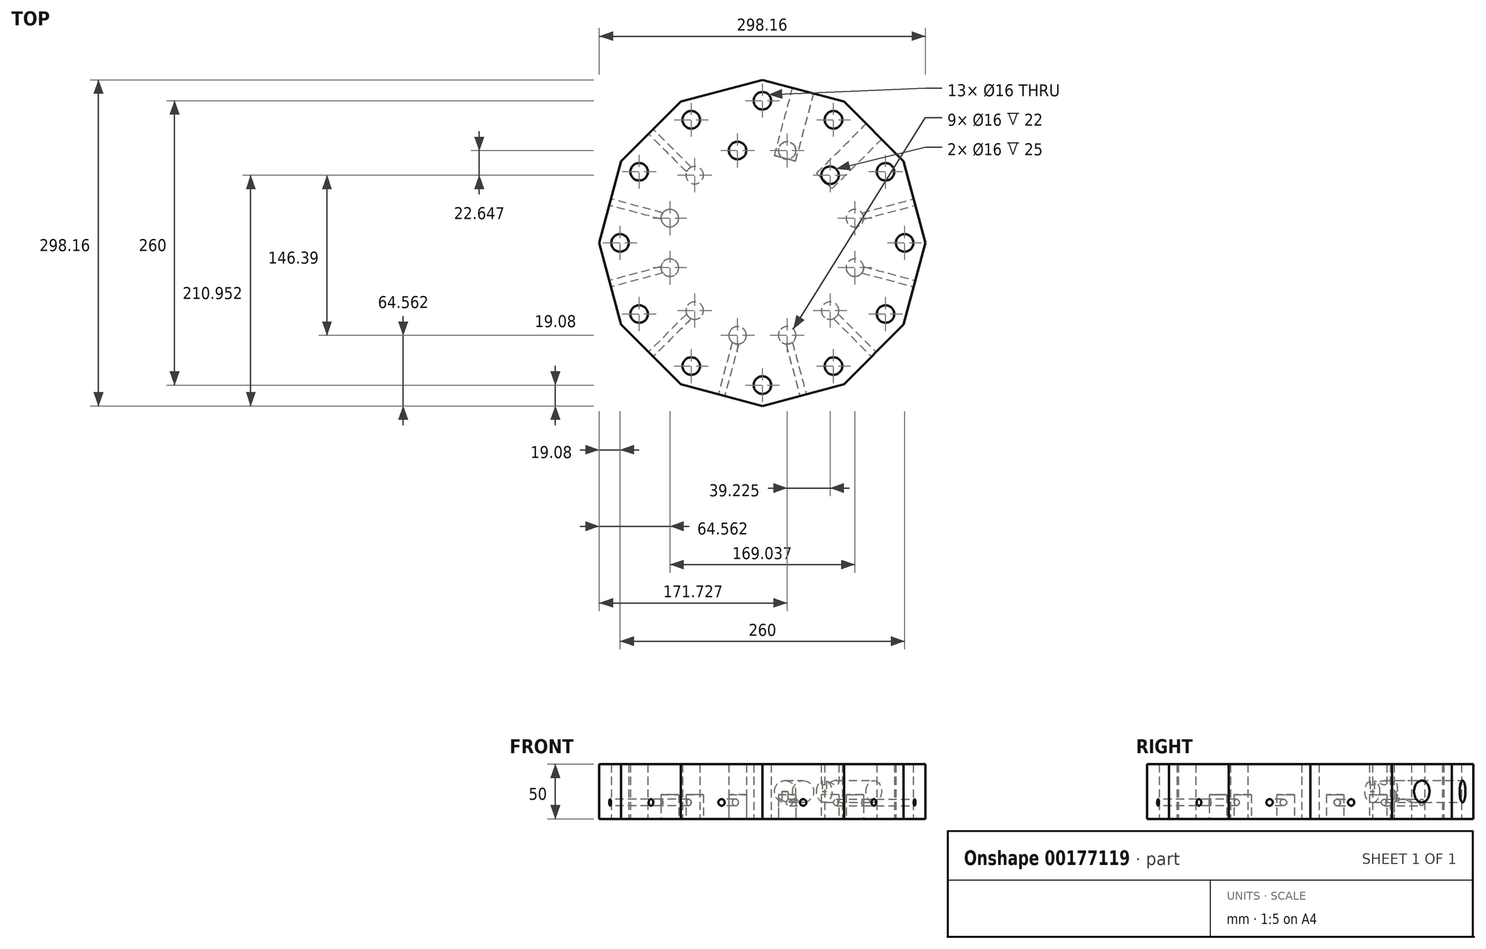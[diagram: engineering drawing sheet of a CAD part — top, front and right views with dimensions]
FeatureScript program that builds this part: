
annotation { "Feature Type Name" : "Feature", "Feature Type Description" : "" }
export const myFeature = defineFeature(function(context is Context, id is Id, definition is map)
    precondition{}
    {
        {
            var Q0;
            Q0=qCreatedBy(makeId("Top.planeOp"),FACE);
            var sketch = newSketch(context, id + "F0", { "sketchPlane" : qUnion([Q0])});
            skCircle(sketch, "E0.cCircle", {"center": v(0, 0) * mm, "radius": 144 * mm, "construction": true});
            skLineSegment(sketch, "E0.0", {"start": v(-74.54, 129.1) * mm, "end": v(0, 149.08) * mm});
            skLineSegment(sketch, "E0.1", {"start": v(0, 149.08) * mm, "end": v(74.54, 129.1) * mm});
            skLineSegment(sketch, "E0.2", {"start": v(74.54, 129.1) * mm, "end": v(129.1, 74.54) * mm});
            skLineSegment(sketch, "E0.3", {"start": v(129.1, 74.54) * mm, "end": v(149.08, 0) * mm});
            skLineSegment(sketch, "E0.4", {"start": v(149.08, 0) * mm, "end": v(129.1, -74.54) * mm});
            skLineSegment(sketch, "E0.5", {"start": v(129.1, -74.54) * mm, "end": v(74.54, -129.1) * mm});
            skLineSegment(sketch, "E0.6", {"start": v(74.54, -129.1) * mm, "end": v(0, -149.08) * mm});
            skLineSegment(sketch, "E0.7", {"start": v(0, -149.08) * mm, "end": v(-74.54, -129.1) * mm});
            skLineSegment(sketch, "E0.8", {"start": v(-74.54, -129.1) * mm, "end": v(-129.1, -74.54) * mm});
            skLineSegment(sketch, "E0.9", {"start": v(-129.1, -74.54) * mm, "end": v(-149.08, 0) * mm});
            skLineSegment(sketch, "E0.10", {"start": v(-149.08, 0) * mm, "end": v(-129.1, 74.54) * mm});
            skLineSegment(sketch, "E0.11", {"start": v(-129.1, 74.54) * mm, "end": v(-74.54, 129.1) * mm});
            skPoint(sketch, "E0.0.midPoint", {"position": v(-37.27, 139.1) * mm});
            skPoint(sketch, "E1.endSnap0", {"position": v(-101.82, 101.82) * mm});
            skSolve(sketch);
        }
        {
            var Q0;
            Q0=makeQuery(id+"F0.imprint","IMPRINT",FACE,{"disambiguationData":[TD([[makeQuery(id+"F0.imprint","IMPRINT",EDGE,{"derivedFrom":sQuery(id+"F0.wireOp",EDGE,"E0.0")}),-1.0]])]});
            extrude(context, id + "F1", {"entities" : qUnion([Q0]), "depth" : 50 * mm});
        }
        {
            var Q0;
            Q0=qCreatedBy(makeId("Top.planeOp"),FACE);
            var sketch = newSketch(context, id + "F2", { "sketchPlane" : qUnion([Q0])});
            skCircle(sketch, "E2", {"center": v(0, 130) * mm, "radius": 8 * mm});
            skCircle(sketch, "E3", {"center": v(22.65, 84.52) * mm, "radius": 8 * mm});
            skLineSegment(sketch, "E4", {"start": v(0, 0) * mm, "end": v(22.65, 84.52) * mm, "construction": true});
            skLineSegment(sketch, "E5", {"start": v(0, 0) * mm, "end": v(-22.65, 84.52) * mm, "construction": true});
            skCircle(sketch, "E6", {"center": v(-22.65, 84.52) * mm, "radius": 8 * mm});
            skCircle(sketch, "E7", {"center": v(61.87, 61.87) * mm, "radius": 8 * mm});
            skLineSegment(sketch, "E8", {"start": v(0, 0) * mm, "end": v(61.87, 61.87) * mm, "construction": true});
            skCircle(sketch, "E9", {"center": v(-61.87, 61.87) * mm, "radius": 8 * mm});
            skLineSegment(sketch, "E10", {"start": v(0, 0) * mm, "end": v(-61.87, 61.87) * mm, "construction": true});
            skCircle(sketch, "E11", {"center": v(0, 0) * mm, "radius": 87.5 * mm, "construction": true});
            skSolve(sketch);
        }
        {
            var Q0;
            Q0=makeQuery(id+"F2.imprint","IMPRINT",FACE,{"disambiguationData":[TD([[makeQuery(id+"F2.imprint","IMPRINT",EDGE,{"derivedFrom":sQuery(id+"F2.wireOp",EDGE,"E2")}),1.0]])]});
            extrude(context, id + "F3", {"entities" : qUnion([Q0]), "depth" : 50 * mm});
        }
        {
            var Q0;
            Q0=makeQuery(id+"F3.opExtrude","SWEPT_BODY",BODY,{"disambiguationData":[OSD([sQuery(id+"F2.wireOp",EDGE,"E2")])]});
            var Q1;
            Q1=sQuery(id+"F0.wireOp",EDGE,"E0.cCircle");
            circularPattern(context, id + "F4", {"entities" : qUnion([Q0]), "axis" : qUnion([Q1]), "angle" : 30 * degree, "instanceCount" : 12});
        }
        {
            var Q0;
            Q0=makeQuery(id+"F2.imprint","IMPRINT",FACE,{"disambiguationData":[TD([[makeQuery(id+"F2.imprint","IMPRINT",EDGE,{"derivedFrom":sQuery(id+"F2.wireOp",EDGE,"E6")}),1.0]])]});
            extrude(context, id + "F5", {"entities" : qUnion([Q0]), "operationType" : NewBodyOperationType.REMOVE, "endBound" : BoundingType.THROUGH_ALL, "depth" : 25 * mm});
        }
        {
            var Q0;
            Q0=makeQuery(id+"F2.imprint","IMPRINT",FACE,{"disambiguationData":[TD([[makeQuery(id+"F2.imprint","IMPRINT",EDGE,{"derivedFrom":sQuery(id+"F2.wireOp",EDGE,"E3")}),1.0]])]});
            extrude(context, id + "F6", {"entities" : qUnion([Q0]), "operationType" : NewBodyOperationType.REMOVE, "depth" : 25 * mm});
        }
        {
            var Q0;
            Q0=makeQuery(id+"F2.imprint","IMPRINT",FACE,{"disambiguationData":[TD([[makeQuery(id+"F2.imprint","IMPRINT",EDGE,{"derivedFrom":sQuery(id+"F2.wireOp",EDGE,"E7")}),1.0]])]});
            extrude(context, id + "F7", {"entities" : qUnion([Q0]), "operationType" : NewBodyOperationType.REMOVE, "depth" : 50 * mm, "hasSecondDirection" : true, "secondDirectionOppositeDirection" : false, "secondDirectionDepth" : 25 * mm});
        }
        {
            var Q0;
            Q0=makeQuery(id+"F4.opPattern","COPY",BODY,{"derivedFrom":makeQuery(id+"F3.opExtrude","SWEPT_BODY",BODY,{"disambiguationData":[OSD([sQuery(id+"F2.wireOp",EDGE,"E2")])]}),"instanceName":"11"});
            var Q1;
            Q1=makeQuery(id+"F4.opPattern","COPY",BODY,{"derivedFrom":makeQuery(id+"F3.opExtrude","SWEPT_BODY",BODY,{"disambiguationData":[OSD([sQuery(id+"F2.wireOp",EDGE,"E2")])]}),"instanceName":"10"});
            var Q2;
            Q2=makeQuery(id+"F4.opPattern","COPY",BODY,{"derivedFrom":makeQuery(id+"F3.opExtrude","SWEPT_BODY",BODY,{"disambiguationData":[OSD([sQuery(id+"F2.wireOp",EDGE,"E2")])]}),"instanceName":"9"});
            var Q3;
            Q3=makeQuery(id+"F4.opPattern","COPY",BODY,{"derivedFrom":makeQuery(id+"F3.opExtrude","SWEPT_BODY",BODY,{"disambiguationData":[OSD([sQuery(id+"F2.wireOp",EDGE,"E2")])]}),"instanceName":"8"});
            var Q4;
            Q4=makeQuery(id+"F4.opPattern","COPY",BODY,{"derivedFrom":makeQuery(id+"F3.opExtrude","SWEPT_BODY",BODY,{"disambiguationData":[OSD([sQuery(id+"F2.wireOp",EDGE,"E2")])]}),"instanceName":"7"});
            var Q5;
            Q5=makeQuery(id+"F4.opPattern","COPY",BODY,{"derivedFrom":makeQuery(id+"F3.opExtrude","SWEPT_BODY",BODY,{"disambiguationData":[OSD([sQuery(id+"F2.wireOp",EDGE,"E2")])]}),"instanceName":"6"});
            var Q6;
            Q6=makeQuery(id+"F4.opPattern","COPY",BODY,{"derivedFrom":makeQuery(id+"F3.opExtrude","SWEPT_BODY",BODY,{"disambiguationData":[OSD([sQuery(id+"F2.wireOp",EDGE,"E2")])]}),"instanceName":"5"});
            var Q7;
            Q7=makeQuery(id+"F4.opPattern","COPY",BODY,{"derivedFrom":makeQuery(id+"F3.opExtrude","SWEPT_BODY",BODY,{"disambiguationData":[OSD([sQuery(id+"F2.wireOp",EDGE,"E2")])]}),"instanceName":"4"});
            var Q8;
            Q8=makeQuery(id+"F4.opPattern","COPY",BODY,{"derivedFrom":makeQuery(id+"F3.opExtrude","SWEPT_BODY",BODY,{"disambiguationData":[OSD([sQuery(id+"F2.wireOp",EDGE,"E2")])]}),"instanceName":"3"});
            var Q9;
            Q9=makeQuery(id+"F4.opPattern","COPY",BODY,{"derivedFrom":makeQuery(id+"F3.opExtrude","SWEPT_BODY",BODY,{"disambiguationData":[OSD([sQuery(id+"F2.wireOp",EDGE,"E2")])]}),"instanceName":"2"});
            var Q10;
            Q10=makeQuery(id+"F4.opPattern","COPY",BODY,{"derivedFrom":makeQuery(id+"F3.opExtrude","SWEPT_BODY",BODY,{"disambiguationData":[OSD([sQuery(id+"F2.wireOp",EDGE,"E2")])]}),"instanceName":"1"});
            var Q11;
            Q11=makeQuery(id+"F3.opExtrude","SWEPT_BODY",BODY,{"disambiguationData":[OSD([sQuery(id+"F2.wireOp",EDGE,"E2")])]});
            var Q12;
            Q12=makeQuery(id+"FBsRg0TL2h17wES_2.opPattern","COPY",BODY,{"derivedFrom":makeQuery(id+"FloVHYxQ3IDST4M_1.opRevolve","SWEPT_BODY",BODY,{"disambiguationData":[OSD([sQuery(id+"FTWyRQ9hsPiHUXF_1.wireOp",EDGE,"gz86ioHb-P1qW-ang3-GePB-rddx3RvaeM8G"),sQuery(id+"FTWyRQ9hsPiHUXF_1.wireOp",EDGE,"9s4MmS5F-P29b-mFub-vPlP-xrfaxyTz5IiV"),sQuery(id+"FTWyRQ9hsPiHUXF_1.wireOp",EDGE,"ncLqOzuC-NzLh-Ri5l-9KgU-PrjhPgCbsoXL"),sQuery(id+"FTWyRQ9hsPiHUXF_1.wireOp",EDGE,"QWZmu36O-cUKC-ijbu-LDt6-pPJv8b1BSPT7"),sQuery(id+"FTWyRQ9hsPiHUXF_1.wireOp",EDGE,"U38Iat36-SeyG-4MAB-tlqH-BICu5RhWfs5p"),sQuery(id+"FTWyRQ9hsPiHUXF_1.wireOp",EDGE,"ujRQtfkf-Bo7a-oEIA-ZBmy-LZaghkBHRdtm")])]}),"instanceName":"8"});
            var Q13;
            Q13=makeQuery(id+"FBsRg0TL2h17wES_2.opPattern","COPY",BODY,{"derivedFrom":makeQuery(id+"FloVHYxQ3IDST4M_1.opRevolve","SWEPT_BODY",BODY,{"disambiguationData":[OSD([sQuery(id+"FTWyRQ9hsPiHUXF_1.wireOp",EDGE,"gz86ioHb-P1qW-ang3-GePB-rddx3RvaeM8G"),sQuery(id+"FTWyRQ9hsPiHUXF_1.wireOp",EDGE,"9s4MmS5F-P29b-mFub-vPlP-xrfaxyTz5IiV"),sQuery(id+"FTWyRQ9hsPiHUXF_1.wireOp",EDGE,"ncLqOzuC-NzLh-Ri5l-9KgU-PrjhPgCbsoXL"),sQuery(id+"FTWyRQ9hsPiHUXF_1.wireOp",EDGE,"QWZmu36O-cUKC-ijbu-LDt6-pPJv8b1BSPT7"),sQuery(id+"FTWyRQ9hsPiHUXF_1.wireOp",EDGE,"U38Iat36-SeyG-4MAB-tlqH-BICu5RhWfs5p"),sQuery(id+"FTWyRQ9hsPiHUXF_1.wireOp",EDGE,"ujRQtfkf-Bo7a-oEIA-ZBmy-LZaghkBHRdtm")])]}),"instanceName":"7"});
            var Q14;
            Q14=makeQuery(id+"FBsRg0TL2h17wES_2.opPattern","COPY",BODY,{"derivedFrom":makeQuery(id+"FloVHYxQ3IDST4M_1.opRevolve","SWEPT_BODY",BODY,{"disambiguationData":[OSD([sQuery(id+"FTWyRQ9hsPiHUXF_1.wireOp",EDGE,"gz86ioHb-P1qW-ang3-GePB-rddx3RvaeM8G"),sQuery(id+"FTWyRQ9hsPiHUXF_1.wireOp",EDGE,"9s4MmS5F-P29b-mFub-vPlP-xrfaxyTz5IiV"),sQuery(id+"FTWyRQ9hsPiHUXF_1.wireOp",EDGE,"ncLqOzuC-NzLh-Ri5l-9KgU-PrjhPgCbsoXL"),sQuery(id+"FTWyRQ9hsPiHUXF_1.wireOp",EDGE,"QWZmu36O-cUKC-ijbu-LDt6-pPJv8b1BSPT7"),sQuery(id+"FTWyRQ9hsPiHUXF_1.wireOp",EDGE,"U38Iat36-SeyG-4MAB-tlqH-BICu5RhWfs5p"),sQuery(id+"FTWyRQ9hsPiHUXF_1.wireOp",EDGE,"ujRQtfkf-Bo7a-oEIA-ZBmy-LZaghkBHRdtm")])]}),"instanceName":"6"});
            var Q15;
            Q15=makeQuery(id+"FBsRg0TL2h17wES_2.opPattern","COPY",BODY,{"derivedFrom":makeQuery(id+"FloVHYxQ3IDST4M_1.opRevolve","SWEPT_BODY",BODY,{"disambiguationData":[OSD([sQuery(id+"FTWyRQ9hsPiHUXF_1.wireOp",EDGE,"gz86ioHb-P1qW-ang3-GePB-rddx3RvaeM8G"),sQuery(id+"FTWyRQ9hsPiHUXF_1.wireOp",EDGE,"9s4MmS5F-P29b-mFub-vPlP-xrfaxyTz5IiV"),sQuery(id+"FTWyRQ9hsPiHUXF_1.wireOp",EDGE,"ncLqOzuC-NzLh-Ri5l-9KgU-PrjhPgCbsoXL"),sQuery(id+"FTWyRQ9hsPiHUXF_1.wireOp",EDGE,"QWZmu36O-cUKC-ijbu-LDt6-pPJv8b1BSPT7"),sQuery(id+"FTWyRQ9hsPiHUXF_1.wireOp",EDGE,"U38Iat36-SeyG-4MAB-tlqH-BICu5RhWfs5p"),sQuery(id+"FTWyRQ9hsPiHUXF_1.wireOp",EDGE,"ujRQtfkf-Bo7a-oEIA-ZBmy-LZaghkBHRdtm")])]}),"instanceName":"5"});
            var Q16;
            Q16=makeQuery(id+"FBsRg0TL2h17wES_2.opPattern","COPY",BODY,{"derivedFrom":makeQuery(id+"FloVHYxQ3IDST4M_1.opRevolve","SWEPT_BODY",BODY,{"disambiguationData":[OSD([sQuery(id+"FTWyRQ9hsPiHUXF_1.wireOp",EDGE,"gz86ioHb-P1qW-ang3-GePB-rddx3RvaeM8G"),sQuery(id+"FTWyRQ9hsPiHUXF_1.wireOp",EDGE,"9s4MmS5F-P29b-mFub-vPlP-xrfaxyTz5IiV"),sQuery(id+"FTWyRQ9hsPiHUXF_1.wireOp",EDGE,"ncLqOzuC-NzLh-Ri5l-9KgU-PrjhPgCbsoXL"),sQuery(id+"FTWyRQ9hsPiHUXF_1.wireOp",EDGE,"QWZmu36O-cUKC-ijbu-LDt6-pPJv8b1BSPT7"),sQuery(id+"FTWyRQ9hsPiHUXF_1.wireOp",EDGE,"U38Iat36-SeyG-4MAB-tlqH-BICu5RhWfs5p"),sQuery(id+"FTWyRQ9hsPiHUXF_1.wireOp",EDGE,"ujRQtfkf-Bo7a-oEIA-ZBmy-LZaghkBHRdtm")])]}),"instanceName":"4"});
            var Q17;
            Q17=makeQuery(id+"FBsRg0TL2h17wES_2.opPattern","COPY",BODY,{"derivedFrom":makeQuery(id+"FloVHYxQ3IDST4M_1.opRevolve","SWEPT_BODY",BODY,{"disambiguationData":[OSD([sQuery(id+"FTWyRQ9hsPiHUXF_1.wireOp",EDGE,"gz86ioHb-P1qW-ang3-GePB-rddx3RvaeM8G"),sQuery(id+"FTWyRQ9hsPiHUXF_1.wireOp",EDGE,"9s4MmS5F-P29b-mFub-vPlP-xrfaxyTz5IiV"),sQuery(id+"FTWyRQ9hsPiHUXF_1.wireOp",EDGE,"ncLqOzuC-NzLh-Ri5l-9KgU-PrjhPgCbsoXL"),sQuery(id+"FTWyRQ9hsPiHUXF_1.wireOp",EDGE,"QWZmu36O-cUKC-ijbu-LDt6-pPJv8b1BSPT7"),sQuery(id+"FTWyRQ9hsPiHUXF_1.wireOp",EDGE,"U38Iat36-SeyG-4MAB-tlqH-BICu5RhWfs5p"),sQuery(id+"FTWyRQ9hsPiHUXF_1.wireOp",EDGE,"ujRQtfkf-Bo7a-oEIA-ZBmy-LZaghkBHRdtm")])]}),"instanceName":"3"});
            var Q18;
            Q18=makeQuery(id+"FBsRg0TL2h17wES_2.opPattern","COPY",BODY,{"derivedFrom":makeQuery(id+"FloVHYxQ3IDST4M_1.opRevolve","SWEPT_BODY",BODY,{"disambiguationData":[OSD([sQuery(id+"FTWyRQ9hsPiHUXF_1.wireOp",EDGE,"gz86ioHb-P1qW-ang3-GePB-rddx3RvaeM8G"),sQuery(id+"FTWyRQ9hsPiHUXF_1.wireOp",EDGE,"9s4MmS5F-P29b-mFub-vPlP-xrfaxyTz5IiV"),sQuery(id+"FTWyRQ9hsPiHUXF_1.wireOp",EDGE,"ncLqOzuC-NzLh-Ri5l-9KgU-PrjhPgCbsoXL"),sQuery(id+"FTWyRQ9hsPiHUXF_1.wireOp",EDGE,"QWZmu36O-cUKC-ijbu-LDt6-pPJv8b1BSPT7"),sQuery(id+"FTWyRQ9hsPiHUXF_1.wireOp",EDGE,"U38Iat36-SeyG-4MAB-tlqH-BICu5RhWfs5p"),sQuery(id+"FTWyRQ9hsPiHUXF_1.wireOp",EDGE,"ujRQtfkf-Bo7a-oEIA-ZBmy-LZaghkBHRdtm")])]}),"instanceName":"2"});
            var Q19;
            Q19=makeQuery(id+"FBsRg0TL2h17wES_2.opPattern","COPY",BODY,{"derivedFrom":makeQuery(id+"FloVHYxQ3IDST4M_1.opRevolve","SWEPT_BODY",BODY,{"disambiguationData":[OSD([sQuery(id+"FTWyRQ9hsPiHUXF_1.wireOp",EDGE,"gz86ioHb-P1qW-ang3-GePB-rddx3RvaeM8G"),sQuery(id+"FTWyRQ9hsPiHUXF_1.wireOp",EDGE,"9s4MmS5F-P29b-mFub-vPlP-xrfaxyTz5IiV"),sQuery(id+"FTWyRQ9hsPiHUXF_1.wireOp",EDGE,"ncLqOzuC-NzLh-Ri5l-9KgU-PrjhPgCbsoXL"),sQuery(id+"FTWyRQ9hsPiHUXF_1.wireOp",EDGE,"QWZmu36O-cUKC-ijbu-LDt6-pPJv8b1BSPT7"),sQuery(id+"FTWyRQ9hsPiHUXF_1.wireOp",EDGE,"U38Iat36-SeyG-4MAB-tlqH-BICu5RhWfs5p"),sQuery(id+"FTWyRQ9hsPiHUXF_1.wireOp",EDGE,"ujRQtfkf-Bo7a-oEIA-ZBmy-LZaghkBHRdtm")])]}),"instanceName":"1"});
            var Q20;
            Q20=makeQuery(id+"FloVHYxQ3IDST4M_1.opRevolve","SWEPT_BODY",BODY,{"disambiguationData":[OSD([sQuery(id+"FTWyRQ9hsPiHUXF_1.wireOp",EDGE,"gz86ioHb-P1qW-ang3-GePB-rddx3RvaeM8G"),sQuery(id+"FTWyRQ9hsPiHUXF_1.wireOp",EDGE,"9s4MmS5F-P29b-mFub-vPlP-xrfaxyTz5IiV"),sQuery(id+"FTWyRQ9hsPiHUXF_1.wireOp",EDGE,"ncLqOzuC-NzLh-Ri5l-9KgU-PrjhPgCbsoXL"),sQuery(id+"FTWyRQ9hsPiHUXF_1.wireOp",EDGE,"QWZmu36O-cUKC-ijbu-LDt6-pPJv8b1BSPT7"),sQuery(id+"FTWyRQ9hsPiHUXF_1.wireOp",EDGE,"U38Iat36-SeyG-4MAB-tlqH-BICu5RhWfs5p"),sQuery(id+"FTWyRQ9hsPiHUXF_1.wireOp",EDGE,"ujRQtfkf-Bo7a-oEIA-ZBmy-LZaghkBHRdtm")])]});
            var Q21;
            Q21=makeQuery(id+"F5XMQ9kYz9Nx559_3.opPattern","COPY",BODY,{"derivedFrom":makeQuery(id+"FeyjR4hLGOr5SDe_2.opRevolve","SWEPT_BODY",BODY,{"disambiguationData":[OSD([sQuery(id+"FTWyRQ9hsPiHUXF_1.wireOp",EDGE,"dtWQvKfD-f1vD-lds4-3zzM-ghYFgyczF8K2"),sQuery(id+"FTWyRQ9hsPiHUXF_1.wireOp",EDGE,"NMOQSono-tL7f-zca5-TIex-ZAwahZChzV1C"),sQuery(id+"FTWyRQ9hsPiHUXF_1.wireOp",EDGE,"ncLqOzuC-NzLh-Ri5l-9KgU-PrjhPgCbsoXL"),sQuery(id+"FTWyRQ9hsPiHUXF_1.wireOp",EDGE,"yjVbwrfn-qVzw-1REl-BjoU-Nn2SmOdFzdHC")])]}),"instanceName":"8"});
            var Q22;
            Q22=makeQuery(id+"F5XMQ9kYz9Nx559_3.opPattern","COPY",BODY,{"derivedFrom":makeQuery(id+"FeyjR4hLGOr5SDe_2.opRevolve","SWEPT_BODY",BODY,{"disambiguationData":[OSD([sQuery(id+"FTWyRQ9hsPiHUXF_1.wireOp",EDGE,"dtWQvKfD-f1vD-lds4-3zzM-ghYFgyczF8K2"),sQuery(id+"FTWyRQ9hsPiHUXF_1.wireOp",EDGE,"NMOQSono-tL7f-zca5-TIex-ZAwahZChzV1C"),sQuery(id+"FTWyRQ9hsPiHUXF_1.wireOp",EDGE,"ncLqOzuC-NzLh-Ri5l-9KgU-PrjhPgCbsoXL"),sQuery(id+"FTWyRQ9hsPiHUXF_1.wireOp",EDGE,"yjVbwrfn-qVzw-1REl-BjoU-Nn2SmOdFzdHC")])]}),"instanceName":"7"});
            var Q23;
            Q23=makeQuery(id+"F5XMQ9kYz9Nx559_3.opPattern","COPY",BODY,{"derivedFrom":makeQuery(id+"FeyjR4hLGOr5SDe_2.opRevolve","SWEPT_BODY",BODY,{"disambiguationData":[OSD([sQuery(id+"FTWyRQ9hsPiHUXF_1.wireOp",EDGE,"dtWQvKfD-f1vD-lds4-3zzM-ghYFgyczF8K2"),sQuery(id+"FTWyRQ9hsPiHUXF_1.wireOp",EDGE,"NMOQSono-tL7f-zca5-TIex-ZAwahZChzV1C"),sQuery(id+"FTWyRQ9hsPiHUXF_1.wireOp",EDGE,"ncLqOzuC-NzLh-Ri5l-9KgU-PrjhPgCbsoXL"),sQuery(id+"FTWyRQ9hsPiHUXF_1.wireOp",EDGE,"yjVbwrfn-qVzw-1REl-BjoU-Nn2SmOdFzdHC")])]}),"instanceName":"6"});
            var Q24;
            Q24=makeQuery(id+"F5XMQ9kYz9Nx559_3.opPattern","COPY",BODY,{"derivedFrom":makeQuery(id+"FeyjR4hLGOr5SDe_2.opRevolve","SWEPT_BODY",BODY,{"disambiguationData":[OSD([sQuery(id+"FTWyRQ9hsPiHUXF_1.wireOp",EDGE,"dtWQvKfD-f1vD-lds4-3zzM-ghYFgyczF8K2"),sQuery(id+"FTWyRQ9hsPiHUXF_1.wireOp",EDGE,"NMOQSono-tL7f-zca5-TIex-ZAwahZChzV1C"),sQuery(id+"FTWyRQ9hsPiHUXF_1.wireOp",EDGE,"ncLqOzuC-NzLh-Ri5l-9KgU-PrjhPgCbsoXL"),sQuery(id+"FTWyRQ9hsPiHUXF_1.wireOp",EDGE,"yjVbwrfn-qVzw-1REl-BjoU-Nn2SmOdFzdHC")])]}),"instanceName":"5"});
            var Q25;
            Q25=makeQuery(id+"F5XMQ9kYz9Nx559_3.opPattern","COPY",BODY,{"derivedFrom":makeQuery(id+"FeyjR4hLGOr5SDe_2.opRevolve","SWEPT_BODY",BODY,{"disambiguationData":[OSD([sQuery(id+"FTWyRQ9hsPiHUXF_1.wireOp",EDGE,"dtWQvKfD-f1vD-lds4-3zzM-ghYFgyczF8K2"),sQuery(id+"FTWyRQ9hsPiHUXF_1.wireOp",EDGE,"NMOQSono-tL7f-zca5-TIex-ZAwahZChzV1C"),sQuery(id+"FTWyRQ9hsPiHUXF_1.wireOp",EDGE,"ncLqOzuC-NzLh-Ri5l-9KgU-PrjhPgCbsoXL"),sQuery(id+"FTWyRQ9hsPiHUXF_1.wireOp",EDGE,"yjVbwrfn-qVzw-1REl-BjoU-Nn2SmOdFzdHC")])]}),"instanceName":"4"});
            var Q26;
            Q26=makeQuery(id+"F5XMQ9kYz9Nx559_3.opPattern","COPY",BODY,{"derivedFrom":makeQuery(id+"FeyjR4hLGOr5SDe_2.opRevolve","SWEPT_BODY",BODY,{"disambiguationData":[OSD([sQuery(id+"FTWyRQ9hsPiHUXF_1.wireOp",EDGE,"dtWQvKfD-f1vD-lds4-3zzM-ghYFgyczF8K2"),sQuery(id+"FTWyRQ9hsPiHUXF_1.wireOp",EDGE,"NMOQSono-tL7f-zca5-TIex-ZAwahZChzV1C"),sQuery(id+"FTWyRQ9hsPiHUXF_1.wireOp",EDGE,"ncLqOzuC-NzLh-Ri5l-9KgU-PrjhPgCbsoXL"),sQuery(id+"FTWyRQ9hsPiHUXF_1.wireOp",EDGE,"yjVbwrfn-qVzw-1REl-BjoU-Nn2SmOdFzdHC")])]}),"instanceName":"3"});
            var Q27;
            Q27=makeQuery(id+"F5XMQ9kYz9Nx559_3.opPattern","COPY",BODY,{"derivedFrom":makeQuery(id+"FeyjR4hLGOr5SDe_2.opRevolve","SWEPT_BODY",BODY,{"disambiguationData":[OSD([sQuery(id+"FTWyRQ9hsPiHUXF_1.wireOp",EDGE,"dtWQvKfD-f1vD-lds4-3zzM-ghYFgyczF8K2"),sQuery(id+"FTWyRQ9hsPiHUXF_1.wireOp",EDGE,"NMOQSono-tL7f-zca5-TIex-ZAwahZChzV1C"),sQuery(id+"FTWyRQ9hsPiHUXF_1.wireOp",EDGE,"ncLqOzuC-NzLh-Ri5l-9KgU-PrjhPgCbsoXL"),sQuery(id+"FTWyRQ9hsPiHUXF_1.wireOp",EDGE,"yjVbwrfn-qVzw-1REl-BjoU-Nn2SmOdFzdHC")])]}),"instanceName":"2"});
            var Q28;
            Q28=makeQuery(id+"F5XMQ9kYz9Nx559_3.opPattern","COPY",BODY,{"derivedFrom":makeQuery(id+"FeyjR4hLGOr5SDe_2.opRevolve","SWEPT_BODY",BODY,{"disambiguationData":[OSD([sQuery(id+"FTWyRQ9hsPiHUXF_1.wireOp",EDGE,"dtWQvKfD-f1vD-lds4-3zzM-ghYFgyczF8K2"),sQuery(id+"FTWyRQ9hsPiHUXF_1.wireOp",EDGE,"NMOQSono-tL7f-zca5-TIex-ZAwahZChzV1C"),sQuery(id+"FTWyRQ9hsPiHUXF_1.wireOp",EDGE,"ncLqOzuC-NzLh-Ri5l-9KgU-PrjhPgCbsoXL"),sQuery(id+"FTWyRQ9hsPiHUXF_1.wireOp",EDGE,"yjVbwrfn-qVzw-1REl-BjoU-Nn2SmOdFzdHC")])]}),"instanceName":"1"});
            var Q29;
            Q29=makeQuery(id+"FeyjR4hLGOr5SDe_2.opRevolve","SWEPT_BODY",BODY,{"disambiguationData":[OSD([sQuery(id+"FTWyRQ9hsPiHUXF_1.wireOp",EDGE,"dtWQvKfD-f1vD-lds4-3zzM-ghYFgyczF8K2"),sQuery(id+"FTWyRQ9hsPiHUXF_1.wireOp",EDGE,"NMOQSono-tL7f-zca5-TIex-ZAwahZChzV1C"),sQuery(id+"FTWyRQ9hsPiHUXF_1.wireOp",EDGE,"ncLqOzuC-NzLh-Ri5l-9KgU-PrjhPgCbsoXL"),sQuery(id+"FTWyRQ9hsPiHUXF_1.wireOp",EDGE,"yjVbwrfn-qVzw-1REl-BjoU-Nn2SmOdFzdHC")])]});
            var Q30;
            Q30=makeQuery(id+"F1.opExtrude","SWEPT_BODY",BODY,{"disambiguationData":[OSD([sQuery(id+"F0.wireOp",EDGE,"E0.0"),sQuery(id+"F0.wireOp",EDGE,"E0.1"),sQuery(id+"F0.wireOp",EDGE,"E0.2"),sQuery(id+"F0.wireOp",EDGE,"E0.3"),sQuery(id+"F0.wireOp",EDGE,"E0.4"),sQuery(id+"F0.wireOp",EDGE,"E0.5"),sQuery(id+"F0.wireOp",EDGE,"E0.6"),sQuery(id+"F0.wireOp",EDGE,"E0.7"),sQuery(id+"F0.wireOp",EDGE,"E0.8"),sQuery(id+"F0.wireOp",EDGE,"E0.9"),sQuery(id+"F0.wireOp",EDGE,"E0.10"),sQuery(id+"F0.wireOp",EDGE,"E0.11")])]});
            booleanBodies(context, id + "F8", {"operationType" : BooleanOperationType.SUBTRACTION, "tools" : qUnion([Q0, Q1, Q2, Q3, Q4, Q5, Q6, Q7, Q8, Q9, Q10, Q11, Q12, Q13, Q14, Q15, Q16, Q17, Q18, Q19, Q20, Q21, Q22, Q23, Q24, Q25, Q26, Q27, Q28, Q29]), "targets" : qUnion([Q30])});
        }
        {
            var Q0;
            Q0=makeQuery(id+"F1.opExtrude","SWEPT_FACE",FACE,{"disambiguationData":[OSD([sQuery(id+"F0.wireOp",EDGE,"E0.11")])]});
            var sketch = newSketch(context, id + "F9", { "sketchPlane" : qUnion([Q0])});
            skCircle(sketch, "E12", {"center": v(0, 15) * mm, "radius": 3 * mm});
            skSolve(sketch);
        }
        {
            var Q0;
            Q0=makeQuery(id+"F9.imprint","IMPRINT",FACE,{"disambiguationData":[TD([[makeQuery(id+"F9.imprint","IMPRINT",EDGE,{"derivedFrom":sQuery(id+"F9.wireOp",EDGE,"E12")}),1.0]])]});
            extrude(context, id + "F10", {"entities" : qUnion([Q0]), "endBound" : BoundingType.SYMMETRIC, "oppositeDirection" : true, "depth" : 120 * mm});
        }
        {
            var Q0;
            Q0=makeQuery(id+"F2.imprint","IMPRINT",FACE,{"disambiguationData":[TD([[makeQuery(id+"F2.imprint","IMPRINT",EDGE,{"derivedFrom":sQuery(id+"F2.wireOp",EDGE,"E9")}),1.0]])]});
            extrude(context, id + "F11", {"entities" : qUnion([Q0]), "endBound" : BoundingType.SYMMETRIC, "depth" : 44 * mm});
        }
        {
            var Q0;
            Q0=makeQuery(id+"F10.opExtrude","SWEPT_BODY",BODY,{"disambiguationData":[OSD([sQuery(id+"F9.wireOp",EDGE,"E12")])]});
            var Q1;
            Q1=makeQuery(id+"F11.opExtrude","SWEPT_BODY",BODY,{"disambiguationData":[OSD([sQuery(id+"F2.wireOp",EDGE,"E9")])]});
            var Q2;
            Q2=sQuery(id+"F0.wireOp",EDGE,"E0.cCircle");
            circularPattern(context, id + "F12", {"entities" : qUnion([Q0, Q1]), "axis" : qUnion([Q2]), "angle" : 30 * degree, "instanceCount" : 9});
        }
        {
            var Q0;
            Q0=makeQuery(id+"F10.opExtrude","SWEPT_BODY",BODY,{"disambiguationData":[OSD([sQuery(id+"F9.wireOp",EDGE,"E12")])]});
            var Q1;
            Q1=makeQuery(id+"F11.opExtrude","SWEPT_BODY",BODY,{"disambiguationData":[OSD([sQuery(id+"F2.wireOp",EDGE,"E9")])]});
            var Q2;
            Q2=makeQuery(id+"F12.opPattern","COPY",BODY,{"derivedFrom":makeQuery(id+"F10.opExtrude","SWEPT_BODY",BODY,{"disambiguationData":[OSD([sQuery(id+"F9.wireOp",EDGE,"E12")])]}),"instanceName":"1"});
            var Q3;
            Q3=makeQuery(id+"F12.opPattern","COPY",BODY,{"derivedFrom":makeQuery(id+"F11.opExtrude","SWEPT_BODY",BODY,{"disambiguationData":[OSD([sQuery(id+"F2.wireOp",EDGE,"E9")])]}),"instanceName":"1"});
            var Q4;
            Q4=makeQuery(id+"F12.opPattern","COPY",BODY,{"derivedFrom":makeQuery(id+"F10.opExtrude","SWEPT_BODY",BODY,{"disambiguationData":[OSD([sQuery(id+"F9.wireOp",EDGE,"E12")])]}),"instanceName":"2"});
            var Q5;
            Q5=makeQuery(id+"F12.opPattern","COPY",BODY,{"derivedFrom":makeQuery(id+"F11.opExtrude","SWEPT_BODY",BODY,{"disambiguationData":[OSD([sQuery(id+"F2.wireOp",EDGE,"E9")])]}),"instanceName":"2"});
            var Q6;
            Q6=makeQuery(id+"F12.opPattern","COPY",BODY,{"derivedFrom":makeQuery(id+"F10.opExtrude","SWEPT_BODY",BODY,{"disambiguationData":[OSD([sQuery(id+"F9.wireOp",EDGE,"E12")])]}),"instanceName":"3"});
            var Q7;
            Q7=makeQuery(id+"F12.opPattern","COPY",BODY,{"derivedFrom":makeQuery(id+"F11.opExtrude","SWEPT_BODY",BODY,{"disambiguationData":[OSD([sQuery(id+"F2.wireOp",EDGE,"E9")])]}),"instanceName":"3"});
            var Q8;
            Q8=makeQuery(id+"F12.opPattern","COPY",BODY,{"derivedFrom":makeQuery(id+"F10.opExtrude","SWEPT_BODY",BODY,{"disambiguationData":[OSD([sQuery(id+"F9.wireOp",EDGE,"E12")])]}),"instanceName":"4"});
            var Q9;
            Q9=makeQuery(id+"F12.opPattern","COPY",BODY,{"derivedFrom":makeQuery(id+"F11.opExtrude","SWEPT_BODY",BODY,{"disambiguationData":[OSD([sQuery(id+"F2.wireOp",EDGE,"E9")])]}),"instanceName":"4"});
            var Q10;
            Q10=makeQuery(id+"F12.opPattern","COPY",BODY,{"derivedFrom":makeQuery(id+"F10.opExtrude","SWEPT_BODY",BODY,{"disambiguationData":[OSD([sQuery(id+"F9.wireOp",EDGE,"E12")])]}),"instanceName":"5"});
            var Q11;
            Q11=makeQuery(id+"F12.opPattern","COPY",BODY,{"derivedFrom":makeQuery(id+"F11.opExtrude","SWEPT_BODY",BODY,{"disambiguationData":[OSD([sQuery(id+"F2.wireOp",EDGE,"E9")])]}),"instanceName":"5"});
            var Q12;
            Q12=makeQuery(id+"F12.opPattern","COPY",BODY,{"derivedFrom":makeQuery(id+"F11.opExtrude","SWEPT_BODY",BODY,{"disambiguationData":[OSD([sQuery(id+"F2.wireOp",EDGE,"E9")])]}),"instanceName":"6"});
            var Q13;
            Q13=makeQuery(id+"F12.opPattern","COPY",BODY,{"derivedFrom":makeQuery(id+"F10.opExtrude","SWEPT_BODY",BODY,{"disambiguationData":[OSD([sQuery(id+"F9.wireOp",EDGE,"E12")])]}),"instanceName":"6"});
            var Q14;
            Q14=makeQuery(id+"F12.opPattern","COPY",BODY,{"derivedFrom":makeQuery(id+"F11.opExtrude","SWEPT_BODY",BODY,{"disambiguationData":[OSD([sQuery(id+"F2.wireOp",EDGE,"E9")])]}),"instanceName":"7"});
            var Q15;
            Q15=makeQuery(id+"F12.opPattern","COPY",BODY,{"derivedFrom":makeQuery(id+"F10.opExtrude","SWEPT_BODY",BODY,{"disambiguationData":[OSD([sQuery(id+"F9.wireOp",EDGE,"E12")])]}),"instanceName":"8"});
            var Q16;
            Q16=makeQuery(id+"F12.opPattern","COPY",BODY,{"derivedFrom":makeQuery(id+"F11.opExtrude","SWEPT_BODY",BODY,{"disambiguationData":[OSD([sQuery(id+"F2.wireOp",EDGE,"E9")])]}),"instanceName":"8"});
            var Q17;
            Q17=makeQuery(id+"F12.opPattern","COPY",BODY,{"derivedFrom":makeQuery(id+"F10.opExtrude","SWEPT_BODY",BODY,{"disambiguationData":[OSD([sQuery(id+"F9.wireOp",EDGE,"E12")])]}),"instanceName":"7"});
            var Q18;
            Q18=makeQuery(id+"F1.opExtrude","SWEPT_BODY",BODY,{"disambiguationData":[OSD([sQuery(id+"F0.wireOp",EDGE,"lc6siBJE-6c1X-ghP5-DSLq-eRXjL7nlxFCf"),sQuery(id+"F0.wireOp",EDGE,"E0.0"),sQuery(id+"F0.wireOp",EDGE,"E0.1"),sQuery(id+"F0.wireOp",EDGE,"E0.2"),sQuery(id+"F0.wireOp",EDGE,"E0.3"),sQuery(id+"F0.wireOp",EDGE,"E0.4"),sQuery(id+"F0.wireOp",EDGE,"E0.5"),sQuery(id+"F0.wireOp",EDGE,"E0.6"),sQuery(id+"F0.wireOp",EDGE,"E0.7"),sQuery(id+"F0.wireOp",EDGE,"E0.8"),sQuery(id+"F0.wireOp",EDGE,"E0.9"),sQuery(id+"F0.wireOp",EDGE,"E0.10"),sQuery(id+"F0.wireOp",EDGE,"E0.11")])]});
            booleanBodies(context, id + "F13", {"operationType" : BooleanOperationType.SUBTRACTION, "tools" : qUnion([Q0, Q1, Q2, Q3, Q4, Q5, Q6, Q7, Q8, Q9, Q10, Q11, Q12, Q13, Q14, Q15, Q16, Q17]), "targets" : qUnion([Q18])});
        }
        {
            var Q0;
            Q0=makeQuery(id+"F1.opExtrude","SWEPT_FACE",FACE,{"disambiguationData":[OSD([sQuery(id+"F0.wireOp",EDGE,"E0.2")])]});
            var sketch = newSketch(context, id + "F14", { "sketchPlane" : qUnion([Q0])});
            skCircle(sketch, "E13", {"center": v(0, 25) * mm, "radius": 10 * mm});
            skSolve(sketch);
        }
        {
            var Q0;
            Q0=makeQuery(id+"F14.imprint","IMPRINT",FACE,{"disambiguationData":[TD([[makeQuery(id+"F14.imprint","IMPRINT",EDGE,{"derivedFrom":sQuery(id+"F14.wireOp",EDGE,"E13")}),1.0]])]});
            extrude(context, id + "F15", {"entities" : qUnion([Q0]), "operationType" : NewBodyOperationType.REMOVE, "oppositeDirection" : true, "depth" : 64 * mm});
        }
        {
            var Q0;
            Q0=makeQuery(id+"F1.opExtrude","SWEPT_FACE",FACE,{"disambiguationData":[OSD([sQuery(id+"F0.wireOp",EDGE,"E0.1")])]});
            var sketch = newSketch(context, id + "F16", { "sketchPlane" : qUnion([Q0])});
            skCircle(sketch, "E14", {"center": v(0, 25) * mm, "radius": 10 * mm});
            skSolve(sketch);
        }
        {
            var Q0;
            Q0=makeQuery(id+"F16.imprint","IMPRINT",FACE,{"disambiguationData":[TD([[makeQuery(id+"F16.imprint","IMPRINT",EDGE,{"derivedFrom":sQuery(id+"F16.wireOp",EDGE,"E14")}),1.0]])]});
            extrude(context, id + "F17", {"entities" : qUnion([Q0]), "operationType" : NewBodyOperationType.REMOVE, "oppositeDirection" : true, "depth" : 64 * mm});
        }
    });
